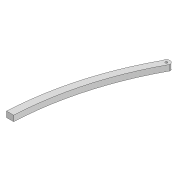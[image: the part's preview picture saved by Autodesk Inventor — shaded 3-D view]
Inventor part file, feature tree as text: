
AUTODESK INVENTOR PART (.ipt)
format: ipt  version: 2022 (Build 260153000, 153)  size: 124,416 bytes
history: native  units: mm
features: sketch x3, extrude x2, fillet x1, projected_geometry x1
ambient origin geometry x8: Origin, YZ Plane, XZ Plane, XY Plane, X Axis, Y Axis, Z Axis, Center Point
bodies: Solid1 (feature_tree)
feature tree (7):
  extrude  "Extrusion1"  Depth=10.0mm
  fillet  "Fillet1"  Radius=3.0mm
  sketch  "Sketch2"  dims[d3=3.0mm d4=8.0mm d5=0.0mm]
  extrude  "Extrusion2"  Depth=8.0mm TaperAngle=0.0deg
  sketch  "Sketch1"  dims[d0=382.775mm d1=10.0mm d2=3.0mm]
  projected_geometry  "Projected Loop1"
  sketch  "Sketch3"  dims[d12=400.0mm d13=400.0mm d14=2.0mm d15=30.0mm d16=180.0mm d17=190.354919mm d18=20.0mm d19=0.0mm]
